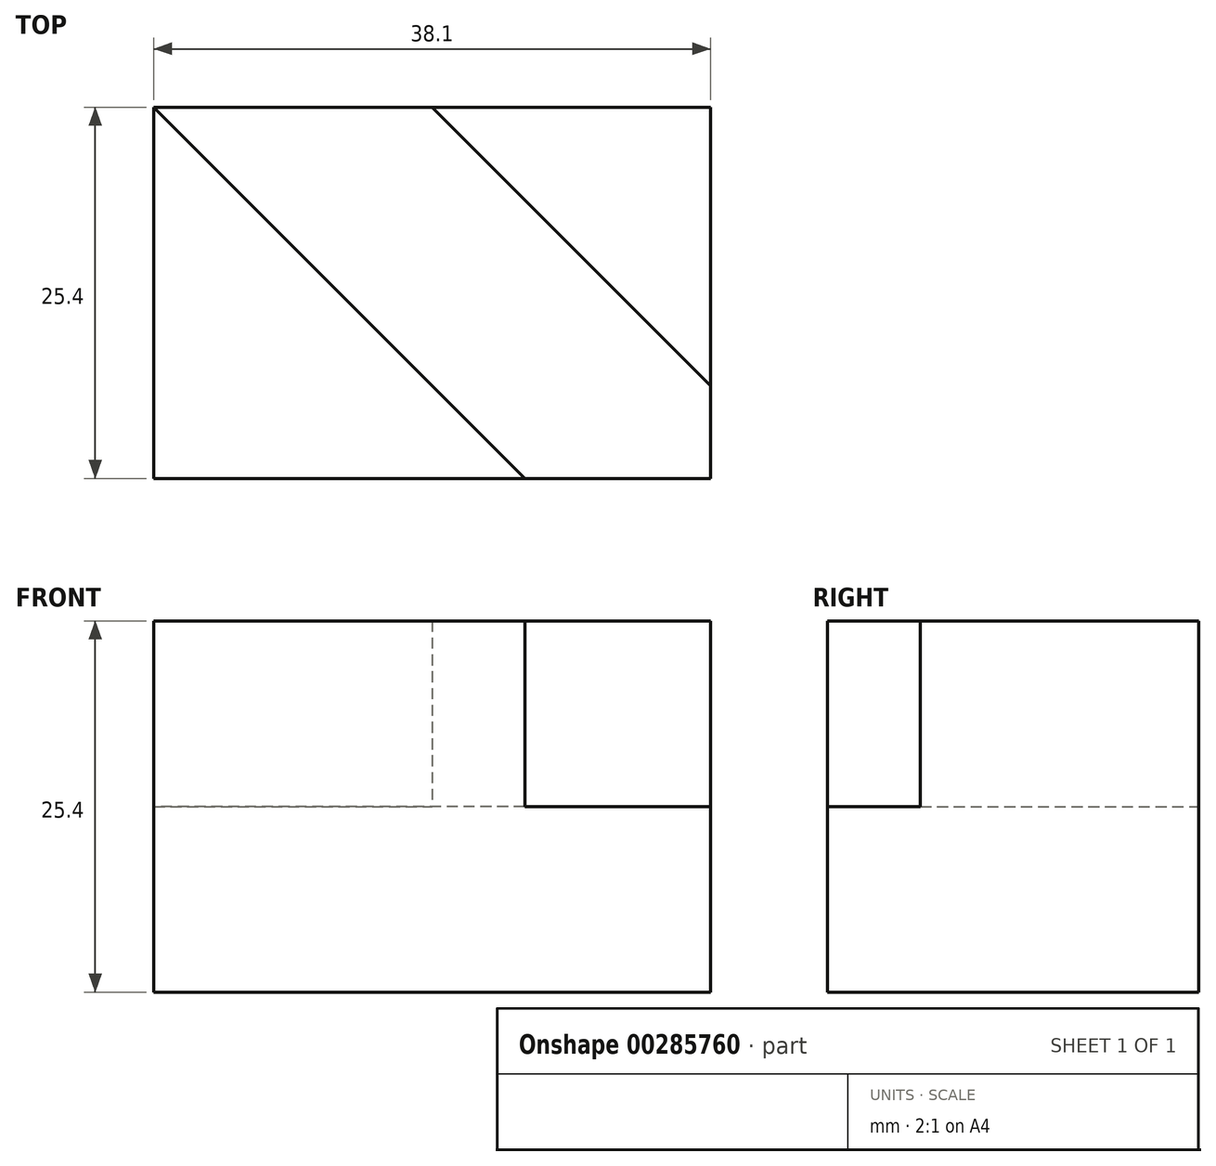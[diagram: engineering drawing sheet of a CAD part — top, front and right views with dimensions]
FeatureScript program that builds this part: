
annotation { "Feature Type Name" : "Feature", "Feature Type Description" : "" }
export const myFeature = defineFeature(function(context is Context, id is Id, definition is map)
    precondition{}
    {
        {
            var Q0;
            Q0=qCreatedBy(makeId("Top.planeOp"),FACE);
            var sketch = newSketch(context, id + "F0", { "sketchPlane" : qUnion([Q0])});
            skLineSegment(sketch, "E0.bottom", {"start": v(0, 0) * mm, "end": v(38.1, 0) * mm});
            skLineSegment(sketch, "E0.top", {"start": v(0, 25.4) * mm, "end": v(38.1, 25.4) * mm});
            skLineSegment(sketch, "E0.left", {"start": v(0, 0) * mm, "end": v(0, 25.4) * mm});
            skLineSegment(sketch, "E0.right", {"start": v(38.1, 0) * mm, "end": v(38.1, 25.4) * mm});
            skLineSegment(sketch, "E1", {"start": v(0, 25.4) * mm, "end": v(25.4, 0) * mm});
            skLineSegment(sketch, "E2", {"start": v(19.05, 25.4) * mm, "end": v(38.1, 6.35) * mm});
            skSolve(sketch);
        }
        {
            var Q0;
            {var subQ3=sQuery(id+"F0.wireOp",EDGE,"E2");Q0=makeQuery(id+"F0.imprint","IMPRINT",FACE,{"disambiguationData":[TD([[makeQuery(id+"F0.imprint","IMPRINT",EDGE,{"derivedFrom":subQ3}),1.0]])]});}
            var Q1;
            {var subQ0=sQuery(id+"F0.wireOp",EDGE,"E0.left");Q1=makeQuery(id+"F0.imprint","IMPRINT",FACE,{"disambiguationData":[TD([[makeQuery(id+"F0.imprint","IMPRINT",EDGE,{"derivedFrom":subQ0}),-1.0]])]});}
            extrude(context, id + "F1", {"entities" : qUnion([Q0, Q1]), "depth" : 25.4 * mm});
        }
        {
            var Q0;
            Q0=makeQuery(id+"F1.opExtrude","CAP_FACE",FACE,{"disambiguationData":[OSD([sQuery(id+"F0.wireOp",EDGE,"E0.bottom"),sQuery(id+"F0.wireOp",EDGE,"E0.top"),sQuery(id+"F0.wireOp",EDGE,"E0.left"),sQuery(id+"F0.wireOp",EDGE,"E0.right")])],"isStart":true});
            var sketch = newSketch(context, id + "F2", { "sketchPlane" : qUnion([Q0])});
            skLineSegment(sketch, "E3.bottom", {"start": v(0, 0) * mm, "end": v(38.1, 0) * mm});
            skLineSegment(sketch, "E3.top", {"start": v(0, -25.4) * mm, "end": v(38.1, -25.4) * mm});
            skLineSegment(sketch, "E3.left", {"start": v(0, -25.4) * mm, "end": v(0, 0) * mm});
            skLineSegment(sketch, "E3.right", {"start": v(38.1, -25.4) * mm, "end": v(38.1, 0) * mm});
            skSolve(sketch);
        }
        {
            var Q0;
            Q0 = qSketchRegion(id + "F2", true);
            extrude(context, id + "F3", {"entities" : qUnion([Q0]), "operationType" : NewBodyOperationType.ADD, "oppositeDirection" : true, "depth" : 12.7 * mm});
        }
    });
